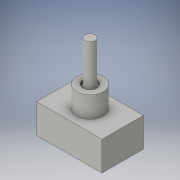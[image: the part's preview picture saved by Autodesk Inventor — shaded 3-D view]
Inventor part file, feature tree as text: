
AUTODESK INVENTOR PART (.ipt)
format: ipt  version: 2016 (Build 200138000, 138)  size: 116,224 bytes
history: native  units: in
note: dims shown in document units (in); Inventor stores cm internally (conversion verified against a paired STEP export)
features: extrude x4, sketch x4
ambient origin geometry x8: Origin, YZ Plane, XZ Plane, XY Plane, X Axis, Y Axis, Z Axis, Center Point
bodies: Solid1 (feature_tree)
feature tree (8):
  extrude  "Extrusion1"  Depth=1.138in
  extrude  "Extrusion2"  Depth=0.722in
  extrude  "Extrusion3"  Depth=0.368in
  extrude  "Extrusion4"  Depth=0.751in
  sketch  "Sketch1"  dims[d0=0.51in d1=1.138in]
  sketch  "Sketch2"  dims[d2=0.722in d3=0.0in d4=0.461in]
  sketch  "Sketch3"  dims[d5=0.368in d6=0.0in d7=0.244in]
  sketch  "Sketch4"  dims[d8=0.05in d9=0.0in d10=0.176in d11=0.751in d12=0.0in]
